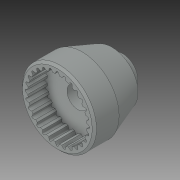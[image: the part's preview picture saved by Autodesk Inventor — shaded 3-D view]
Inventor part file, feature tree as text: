
AUTODESK INVENTOR PART (.ipt)
format: ipt  version: 2019 (Build 230136000, 136)  size: 325,120 bytes
history: native  units: in
note: dims shown in document units (in); Inventor stores cm internally (conversion verified against a paired STEP export)
features: chamfer x1
ambient origin geometry x8: Origin, YZ Plane, XZ Plane, XY Plane, X Axis, Y Axis, Z Axis, Center Point
bodies: Solid1 (feature_tree)
feature tree (1):
  chamfer  "Chamfer1"  [1 undecoded]
note: 1 required parameter value undecoded (feature->parameter linkage not recoverable at this tier; creation-order binding heuristic only, values carry confidence <= 0.55)
